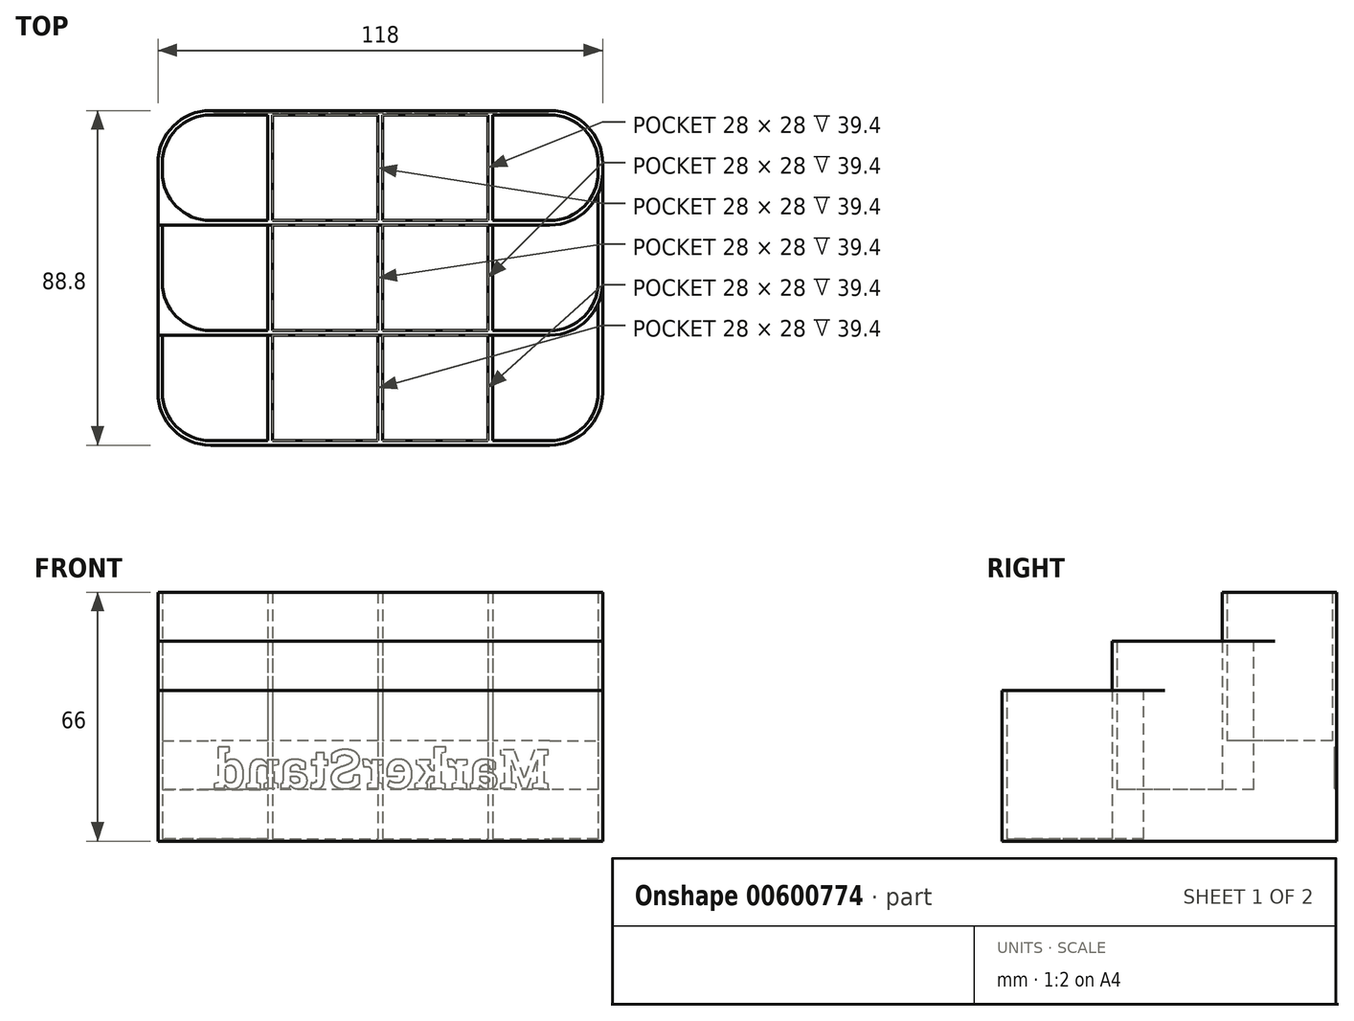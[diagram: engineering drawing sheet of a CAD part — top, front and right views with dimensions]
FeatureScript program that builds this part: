
annotation { "Feature Type Name" : "Feature", "Feature Type Description" : "" }
export const myFeature = defineFeature(function(context is Context, id is Id, definition is map)
    precondition{}
    {
        {
            var Q0;
            Q0=qCreatedBy(makeId("Top.planeOp"),FACE);
            var sketch = newSketch(context, id + "F0", { "sketchPlane" : qUnion([Q0])});
            skLineSegment(sketch, "E0.bottom", {"start": v(59, 44.4) * mm, "end": v(-59, 44.4) * mm});
            skLineSegment(sketch, "E0.top", {"start": v(59, -44.4) * mm, "end": v(-59, -44.4) * mm});
            skLineSegment(sketch, "E0.left", {"start": v(59, 44.4) * mm, "end": v(59, -44.4) * mm});
            skLineSegment(sketch, "E0.right", {"start": v(-59, 44.4) * mm, "end": v(-59, -44.4) * mm});
            skPoint(sketch, "E0.middle", {"position": v(0, 0) * mm});
            skLineSegment(sketch, "E1.bottom", {"start": v(-57.8, -43.2) * mm, "end": v(-29.8, -43.2) * mm});
            skLineSegment(sketch, "E1.top", {"start": v(-57.8, -15.2) * mm, "end": v(-29.8, -15.2) * mm});
            skLineSegment(sketch, "E1.left", {"start": v(-57.8, -43.2) * mm, "end": v(-57.8, -15.2) * mm});
            skLineSegment(sketch, "E1.right", {"start": v(-29.8, -43.2) * mm, "end": v(-29.8, -15.2) * mm});
            skLineSegment(sketch, "E2.0.1.0", {"start": v(-57.8, -14) * mm, "end": v(-57.8, 14) * mm});
            skLineSegment(sketch, "E2.0.1.1", {"start": v(-57.8, -14) * mm, "end": v(-29.8, -14) * mm});
            skLineSegment(sketch, "E2.0.1.2", {"start": v(-29.8, -14) * mm, "end": v(-29.8, 14) * mm});
            skLineSegment(sketch, "E2.0.1.3", {"start": v(-57.8, 14) * mm, "end": v(-29.8, 14) * mm});
            skLineSegment(sketch, "E2.0.2.0", {"start": v(-57.8, 15.2) * mm, "end": v(-57.8, 43.2) * mm});
            skLineSegment(sketch, "E2.0.2.1", {"start": v(-57.8, 15.2) * mm, "end": v(-29.8, 15.2) * mm});
            skLineSegment(sketch, "E2.0.2.2", {"start": v(-29.8, 15.2) * mm, "end": v(-29.8, 43.2) * mm});
            skLineSegment(sketch, "E2.0.2.3", {"start": v(-57.8, 43.2) * mm, "end": v(-29.8, 43.2) * mm});
            skLineSegment(sketch, "E2.1.0.0", {"start": v(-28.6, -43.2) * mm, "end": v(-28.6, -15.2) * mm});
            skLineSegment(sketch, "E2.1.0.1", {"start": v(-28.6, -43.2) * mm, "end": v(-0.6, -43.2) * mm});
            skLineSegment(sketch, "E2.1.0.2", {"start": v(-0.6, -43.2) * mm, "end": v(-0.6, -15.2) * mm});
            skLineSegment(sketch, "E2.1.0.3", {"start": v(-28.6, -15.2) * mm, "end": v(-0.6, -15.2) * mm});
            skLineSegment(sketch, "E2.1.1.0", {"start": v(-28.6, -14) * mm, "end": v(-28.6, 14) * mm});
            skLineSegment(sketch, "E2.1.1.1", {"start": v(-28.6, -14) * mm, "end": v(-0.6, -14) * mm});
            skLineSegment(sketch, "E2.1.1.2", {"start": v(-0.6, -14) * mm, "end": v(-0.6, 14) * mm});
            skLineSegment(sketch, "E2.1.1.3", {"start": v(-28.6, 14) * mm, "end": v(-0.6, 14) * mm});
            skLineSegment(sketch, "E2.1.2.0", {"start": v(-28.6, 15.2) * mm, "end": v(-28.6, 43.2) * mm});
            skLineSegment(sketch, "E2.1.2.1", {"start": v(-28.6, 15.2) * mm, "end": v(-0.6, 15.2) * mm});
            skLineSegment(sketch, "E2.1.2.2", {"start": v(-0.6, 15.2) * mm, "end": v(-0.6, 43.2) * mm});
            skLineSegment(sketch, "E2.1.2.3", {"start": v(-28.6, 43.2) * mm, "end": v(-0.6, 43.2) * mm});
            skLineSegment(sketch, "E2.2.0.0", {"start": v(0.6, -43.2) * mm, "end": v(0.6, -15.2) * mm});
            skLineSegment(sketch, "E2.2.0.1", {"start": v(0.6, -43.2) * mm, "end": v(28.6, -43.2) * mm});
            skLineSegment(sketch, "E2.2.0.2", {"start": v(28.6, -43.2) * mm, "end": v(28.6, -15.2) * mm});
            skLineSegment(sketch, "E2.2.0.3", {"start": v(0.6, -15.2) * mm, "end": v(28.6, -15.2) * mm});
            skLineSegment(sketch, "E2.2.1.0", {"start": v(0.6, -14) * mm, "end": v(0.6, 14) * mm});
            skLineSegment(sketch, "E2.2.1.1", {"start": v(0.6, -14) * mm, "end": v(28.6, -14) * mm});
            skLineSegment(sketch, "E2.2.1.2", {"start": v(28.6, -14) * mm, "end": v(28.6, 14) * mm});
            skLineSegment(sketch, "E2.2.1.3", {"start": v(0.6, 14) * mm, "end": v(28.6, 14) * mm});
            skLineSegment(sketch, "E2.2.2.0", {"start": v(0.6, 15.2) * mm, "end": v(0.6, 43.2) * mm});
            skLineSegment(sketch, "E2.2.2.1", {"start": v(0.6, 15.2) * mm, "end": v(28.6, 15.2) * mm});
            skLineSegment(sketch, "E2.2.2.2", {"start": v(28.6, 15.2) * mm, "end": v(28.6, 43.2) * mm});
            skLineSegment(sketch, "E2.2.2.3", {"start": v(0.6, 43.2) * mm, "end": v(28.6, 43.2) * mm});
            skLineSegment(sketch, "E2.3.0.0", {"start": v(29.8, -43.2) * mm, "end": v(29.8, -15.2) * mm});
            skLineSegment(sketch, "E2.3.0.1", {"start": v(29.8, -43.2) * mm, "end": v(57.8, -43.2) * mm});
            skLineSegment(sketch, "E2.3.0.2", {"start": v(57.8, -43.2) * mm, "end": v(57.8, -15.2) * mm});
            skLineSegment(sketch, "E2.3.0.3", {"start": v(29.8, -15.2) * mm, "end": v(57.8, -15.2) * mm});
            skLineSegment(sketch, "E2.3.1.0", {"start": v(29.8, -14) * mm, "end": v(29.8, 14) * mm});
            skLineSegment(sketch, "E2.3.1.1", {"start": v(29.8, -14) * mm, "end": v(57.8, -14) * mm});
            skLineSegment(sketch, "E2.3.1.2", {"start": v(57.8, -14) * mm, "end": v(57.8, 14) * mm});
            skLineSegment(sketch, "E2.3.1.3", {"start": v(29.8, 14) * mm, "end": v(57.8, 14) * mm});
            skLineSegment(sketch, "E2.3.2.0", {"start": v(29.8, 15.2) * mm, "end": v(29.8, 43.2) * mm});
            skLineSegment(sketch, "E2.3.2.1", {"start": v(29.8, 15.2) * mm, "end": v(57.8, 15.2) * mm});
            skLineSegment(sketch, "E2.3.2.2", {"start": v(57.8, 15.2) * mm, "end": v(57.8, 43.2) * mm});
            skLineSegment(sketch, "E2.3.2.3", {"start": v(29.8, 43.2) * mm, "end": v(57.8, 43.2) * mm});
            skLineSegment(sketch, "E2.direction1", {"start": v(-57.8, -43.2) * mm, "end": v(-28.6, -43.2) * mm, "construction": true});
            skLineSegment(sketch, "E2.direction2", {"start": v(-57.8, -43.2) * mm, "end": v(-57.8, -14) * mm, "construction": true});
            skSolve(sketch);
        }
        {
            var Q0;
            Q0 = qSketchRegion(id + "F0", true);
            extrude(context, id + "F1", {"entities" : qUnion([Q0]), "depth" : 66 * mm, "offsetDistance" : 25 * mm});
        }
        {
            var Q0;
            Q0=makeQuery(id+"F1.opExtrude","SWEPT_FACE",FACE,{"disambiguationData":[OSD([sQuery(id+"F0.wireOp",EDGE,"E0.left")])]});
            var sketch = newSketch(context, id + "F2", { "sketchPlane" : qUnion([Q0])});
            skLineSegment(sketch, "E3", {"start": v(44.4, 0) * mm, "end": v(-44.4, 0) * mm});
            skLineSegment(sketch, "E4", {"start": v(-44.4, 0) * mm, "end": v(-44.4, 0.6) * mm});
            skLineSegment(sketch, "E5", {"start": v(-44.4, 0.6) * mm, "end": v(-15.2, 0.6) * mm});
            skLineSegment(sketch, "E6", {"start": v(-15.2, 0.6) * mm, "end": v(-15.2, 13.6) * mm});
            skLineSegment(sketch, "E7", {"start": v(-15.2, 13.6) * mm, "end": v(14, 13.6) * mm});
            skLineSegment(sketch, "E8", {"start": v(14, 13.6) * mm, "end": v(14, 26.6) * mm});
            skLineSegment(sketch, "E9", {"start": v(14, 26.6) * mm, "end": v(43.2, 26.6) * mm});
            skLineSegment(sketch, "E10", {"start": v(44.4, 26.6) * mm, "end": v(44.4, 0) * mm});
            skLineSegment(sketch, "E11", {"start": v(43.2, 26.6) * mm, "end": v(44.4, 26.6) * mm});
            skSolve(sketch);
        }
        {
            var Q0;
            Q0 = qSketchRegion(id + "F2", true);
            var Q1;
            Q1=makeQuery(id+"F1.opExtrude","SWEPT_FACE",FACE,{"disambiguationData":[OSD([sQuery(id+"F0.wireOp",EDGE,"E0.right")])]});
            extrude(context, id + "F3", {"entities" : qUnion([Q0]), "operationType" : NewBodyOperationType.ADD, "endBound" : BoundingType.UP_TO_SURFACE, "oppositeDirection" : true, "depth" : 25 * mm, "endBoundEntityFace" : qUnion([Q1]), "offsetDistance" : 25 * mm});
        }
        {
            var Q0;
            Q0=makeQuery(id+"F1.opExtrude","SWEPT_FACE",FACE,{"disambiguationData":[OSD([sQuery(id+"F0.wireOp",EDGE,"E0.right")])]});
            var sketch = newSketch(context, id + "F4", { "sketchPlane" : qUnion([Q0])});
            skLineSegment(sketch, "E12", {"start": v(44.4, 66) * mm, "end": v(44.4, 40) * mm});
            skLineSegment(sketch, "E13", {"start": v(44.4, 40) * mm, "end": v(15.2, 40) * mm});
            skLineSegment(sketch, "E14", {"start": v(15.2, 40) * mm, "end": v(15.2, 53) * mm});
            skLineSegment(sketch, "E15", {"start": v(15.2, 53) * mm, "end": v(-14, 53) * mm});
            skLineSegment(sketch, "E16", {"start": v(-14, 53) * mm, "end": v(-14, 66) * mm});
            skLineSegment(sketch, "E17", {"start": v(-14, 66) * mm, "end": v(44.4, 66) * mm});
            skSolve(sketch);
        }
        {
            var Q0;
            Q0 = qSketchRegion(id + "F4", true);
            extrude(context, id + "F5", {"entities" : qUnion([Q0]), "operationType" : NewBodyOperationType.REMOVE, "endBound" : BoundingType.THROUGH_ALL, "oppositeDirection" : true, "depth" : 25 * mm, "offsetDistance" : 25 * mm});
        }
        {
            var Q0;
            Q0=makeQuery(id+"F1.opExtrude","SWEPT_EDGE",EDGE,{"disambiguationData":[OSD([sQuery(id+"F0.wireOp",EDGE,"E2.6.3.2"),sQuery(id+"F0.wireOp",EDGE,"E2.6.3.3")])]});
            var Q1;
            Q1=makeQuery(id+"F1.opExtrude","SWEPT_EDGE",EDGE,{"disambiguationData":[OSD([sQuery(id+"F0.wireOp",EDGE,"E2.0.3.0"),sQuery(id+"F0.wireOp",EDGE,"E2.0.3.3")])]});
            var Q2;
            Q2=makeQuery(id+"F1.opExtrude","SWEPT_EDGE",EDGE,{"disambiguationData":[OSD([sQuery(id+"F0.wireOp",EDGE,"E2.6.0.1"),sQuery(id+"F0.wireOp",EDGE,"E2.6.0.2")])]});
            var Q3;
            Q3=makeQuery(id+"F1.opExtrude","SWEPT_EDGE",EDGE,{"disambiguationData":[OSD([sQuery(id+"F0.wireOp",EDGE,"E1.bottom"),sQuery(id+"F0.wireOp",EDGE,"E1.left")])]});
            var Q4;
            Q4=makeQuery(id+"F1.opExtrude","SWEPT_EDGE",EDGE,{"disambiguationData":[OSD([sQuery(id+"F0.wireOp",EDGE,"E2.6.1.1"),sQuery(id+"F0.wireOp",EDGE,"E2.6.1.2")])]});
            var Q5;
            Q5=makeQuery(id+"F1.opExtrude","SWEPT_EDGE",EDGE,{"disambiguationData":[OSD([sQuery(id+"F0.wireOp",EDGE,"E2.6.2.1"),sQuery(id+"F0.wireOp",EDGE,"E2.6.2.2")])]});
            var Q6;
            Q6=makeQuery(id+"F1.opExtrude","SWEPT_EDGE",EDGE,{"disambiguationData":[OSD([sQuery(id+"F0.wireOp",EDGE,"E2.0.2.0"),sQuery(id+"F0.wireOp",EDGE,"E2.0.2.1")])]});
            var Q7;
            Q7=makeQuery(id+"F1.opExtrude","SWEPT_EDGE",EDGE,{"disambiguationData":[OSD([sQuery(id+"F0.wireOp",EDGE,"E2.0.1.0"),sQuery(id+"F0.wireOp",EDGE,"E2.0.1.1")])]});
            var Q8;
            Q8=makeQuery(id+"F1.opExtrude","SWEPT_EDGE",EDGE,{"disambiguationData":[OSD([sQuery(id+"F0.wireOp",EDGE,"E2.6.3.1"),sQuery(id+"F0.wireOp",EDGE,"E2.6.3.2")])]});
            var Q9;
            Q9=makeQuery(id+"F1.opExtrude","SWEPT_EDGE",EDGE,{"disambiguationData":[OSD([sQuery(id+"F0.wireOp",EDGE,"E2.0.3.0"),sQuery(id+"F0.wireOp",EDGE,"E2.0.3.1")])]});
            var Q10;
            Q10=makeQuery(id+"F1.opExtrude","SWEPT_EDGE",EDGE,{"disambiguationData":[OSD([sQuery(id+"F0.wireOp",EDGE,"E2.3.1.1"),sQuery(id+"F0.wireOp",EDGE,"E2.3.1.2")])]});
            var Q11;
            Q11=makeQuery(id+"F1.opExtrude","SWEPT_EDGE",EDGE,{"disambiguationData":[OSD([sQuery(id+"F0.wireOp",EDGE,"E2.3.0.1"),sQuery(id+"F0.wireOp",EDGE,"E2.3.0.2")])]});
            var Q12;
            Q12=makeQuery(id+"F1.opExtrude","SWEPT_EDGE",EDGE,{"disambiguationData":[OSD([sQuery(id+"F0.wireOp",EDGE,"E2.3.2.1"),sQuery(id+"F0.wireOp",EDGE,"E2.3.2.2")])]});
            var Q13;
            Q13=makeQuery(id+"F1.opExtrude","SWEPT_EDGE",EDGE,{"disambiguationData":[OSD([sQuery(id+"F0.wireOp",EDGE,"E2.3.2.2"),sQuery(id+"F0.wireOp",EDGE,"E2.3.2.3")])]});
            var Q14;
            Q14=makeQuery(id+"F1.opExtrude","SWEPT_EDGE",EDGE,{"disambiguationData":[OSD([sQuery(id+"F0.wireOp",EDGE,"E2.0.2.0"),sQuery(id+"F0.wireOp",EDGE,"E2.0.2.3")])]});
            fillet(context, id + "F6", {"entities" : qUnion([Q0, Q1, Q2, Q3, Q4, Q5, Q6, Q7, Q8, Q9, Q10, Q11, Q12, Q13, Q14]), "radius" : 12.8 * mm, "tangentPropagation" : true, "allowEdgeOverflow" : false});
        }
        {
            var Q0;
            Q0=makeQuery(id+"F5.boolean.opBoolean","COPY",EDGE,{"derivedFrom":makeQuery(id+"F5.opExtrude","CAP_EDGE",EDGE,{"disambiguationData":[OSD([sQuery(id+"F4.wireOp",EDGE,"E16")])],"isStart":true})});
            var Q1;
            Q1=makeQuery(id+"F1.opExtrude","SWEPT_EDGE",EDGE,{"disambiguationData":[OSD([sQuery(id+"F0.wireOp",EDGE,"E0.bottom"),sQuery(id+"F0.wireOp",EDGE,"E0.right")])]});
            var Q2;
            Q2=makeQuery(id+"F1.opExtrude","SWEPT_EDGE",EDGE,{"disambiguationData":[OSD([sQuery(id+"F0.wireOp",EDGE,"E0.bottom"),sQuery(id+"F0.wireOp",EDGE,"E0.left")])]});
            var Q3;
            Q3=makeQuery(id+"F5.boolean.opBoolean","INTERSECT",EDGE,{"derivedFrom":[makeQuery(id+"F1.opExtrude","SWEPT_FACE",FACE,{"disambiguationData":[OSD([sQuery(id+"F0.wireOp",EDGE,"E0.left")])]}),makeQuery(id+"F5.opExtrude","SWEPT_FACE",FACE,{"disambiguationData":[OSD([sQuery(id+"F4.wireOp",EDGE,"E16")])]})]});
            var Q4;
            Q4=makeQuery(id+"F5.boolean.opBoolean","INTERSECT",EDGE,{"derivedFrom":[makeQuery(id+"F1.opExtrude","SWEPT_FACE",FACE,{"disambiguationData":[OSD([sQuery(id+"F0.wireOp",EDGE,"E0.left")])]}),makeQuery(id+"F5.opExtrude","SWEPT_FACE",FACE,{"disambiguationData":[OSD([sQuery(id+"F4.wireOp",EDGE,"E14")])]})]});
            var Q5;
            Q5=makeQuery(id+"F1.opExtrude","SWEPT_EDGE",EDGE,{"disambiguationData":[OSD([sQuery(id+"F0.wireOp",EDGE,"E0.top"),sQuery(id+"F0.wireOp",EDGE,"E0.left")])]});
            var Q6;
            Q6=makeQuery(id+"F1.opExtrude","SWEPT_EDGE",EDGE,{"disambiguationData":[OSD([sQuery(id+"F0.wireOp",EDGE,"E0.top"),sQuery(id+"F0.wireOp",EDGE,"E0.right")])]});
            var Q7;
            Q7=makeQuery(id+"F5.boolean.opBoolean","COPY",EDGE,{"derivedFrom":makeQuery(id+"F5.opExtrude","CAP_EDGE",EDGE,{"disambiguationData":[OSD([sQuery(id+"F4.wireOp",EDGE,"E14")])],"isStart":true})});
            fillet(context, id + "F7", {"entities" : qUnion([Q0, Q1, Q2, Q3, Q4, Q5, Q6, Q7]), "radius" : 14 * mm, "tangentPropagation" : true, "allowEdgeOverflow" : false});
        }
        {
            var Q0;
            Q0=makeQuery(id+"F1.opExtrude","SWEPT_FACE",FACE,{"disambiguationData":[OSD([sQuery(id+"F0.wireOp",EDGE,"E0.bottom")])]});
            var sketch = newSketch(context, id + "F8", { "sketchPlane" : qUnion([Q0])});
            skLineSegment(sketch, "E18", {"start": v(0, 0) * mm, "end": v(0, 66) * mm, "construction": true});
            skText(sketch, "E19", { "text": "MarkerStand", "fontName": "RobotoSlab-Bold.ttf"});
            const initialGuessF8  = {"E19": [-0.045, 0.014, 1, 0, 0.01032]};
            skSetInitialGuess(sketch, initialGuessF8);
            skSolve(sketch);
        }
        {
            var Q0;
            Q0 = qSketchRegion(id + "F8", true);
            extrude(context, id + "F9", {"entities" : qUnion([Q0]), "operationType" : NewBodyOperationType.REMOVE, "oppositeDirection" : true, "depth" : 0.6 * mm, "offsetDistance" : 25 * mm});
        }
    });
